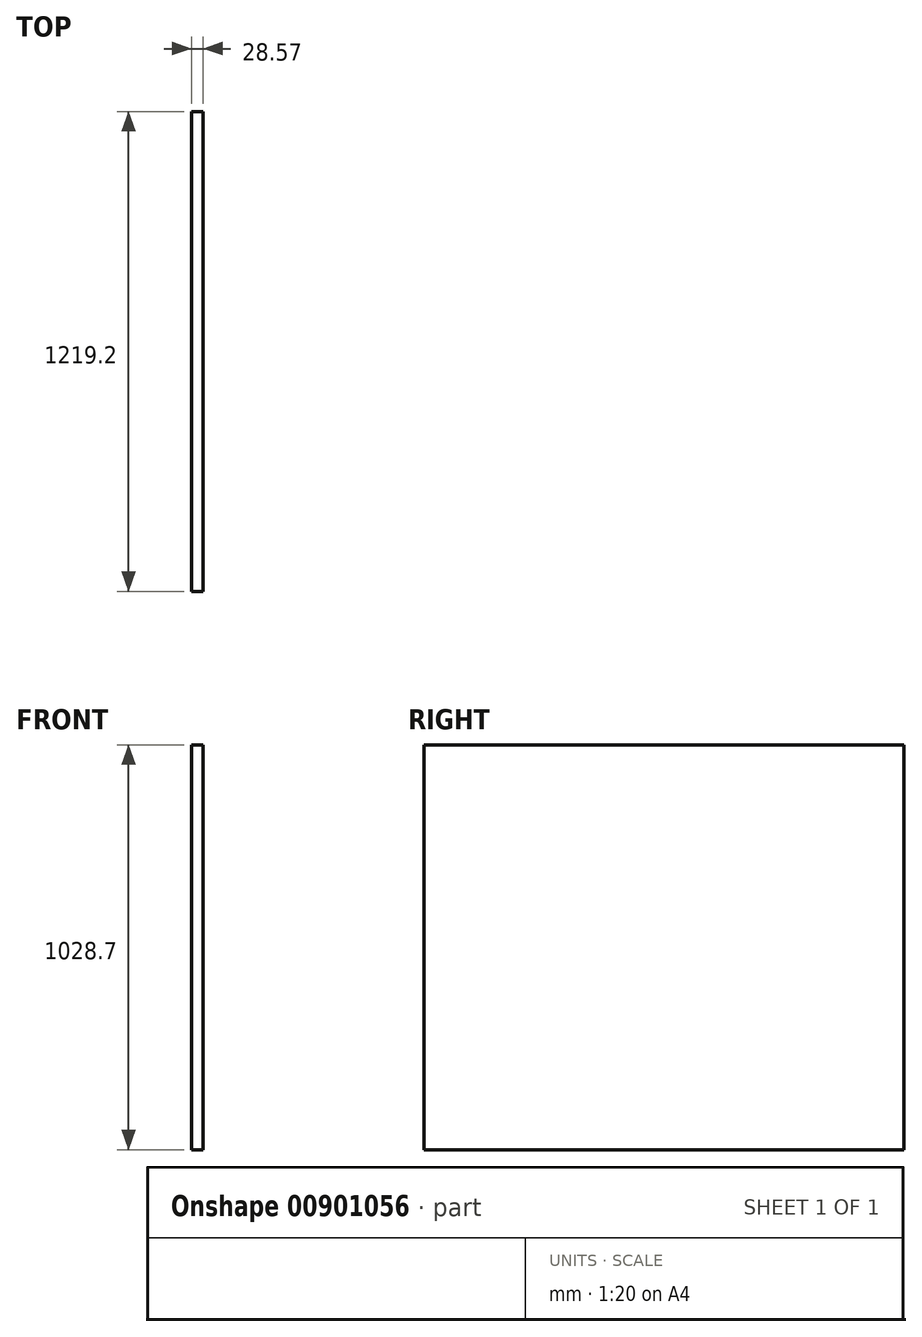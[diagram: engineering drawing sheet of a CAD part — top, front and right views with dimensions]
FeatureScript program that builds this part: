
annotation { "Feature Type Name" : "Feature", "Feature Type Description" : "" }
export const myFeature = defineFeature(function(context is Context, id is Id, definition is map)
    precondition{}
    {
        {
            var Q0;
            Q0=qCreatedBy(makeId("Right.planeOp"),FACE);
            var sketch = newSketch(context, id + "F0", { "sketchPlane" : qUnion([Q0])});
            skLineSegment(sketch, "E0.bottom", {"start": v(609.6, 514.35) * mm, "end": v(-609.6, 514.35) * mm});
            skLineSegment(sketch, "E0.top", {"start": v(609.6, -514.35) * mm, "end": v(-609.6, -514.35) * mm});
            skLineSegment(sketch, "E0.left", {"start": v(609.6, 514.35) * mm, "end": v(609.6, -514.35) * mm});
            skLineSegment(sketch, "E0.right", {"start": v(-609.6, 514.35) * mm, "end": v(-609.6, -514.35) * mm});
            skPoint(sketch, "E0.middle", {"position": v(0, 0) * mm});
            skSolve(sketch);
        }
        {
            var Q0;
            Q0=makeQuery(id+"F0.imprint","IMPRINT",FACE,{"disambiguationData":[TD([[makeQuery(id+"F0.imprint","IMPRINT",EDGE,{"derivedFrom":sQuery(id+"F0.wireOp",EDGE,"E0.bottom")}),1.0]])]});
            extrude(context, id + "F1", {"entities" : qUnion([Q0]), "depth" : 28.57 * mm, "offsetDistance" : 25.4 * mm});
        }
    });
